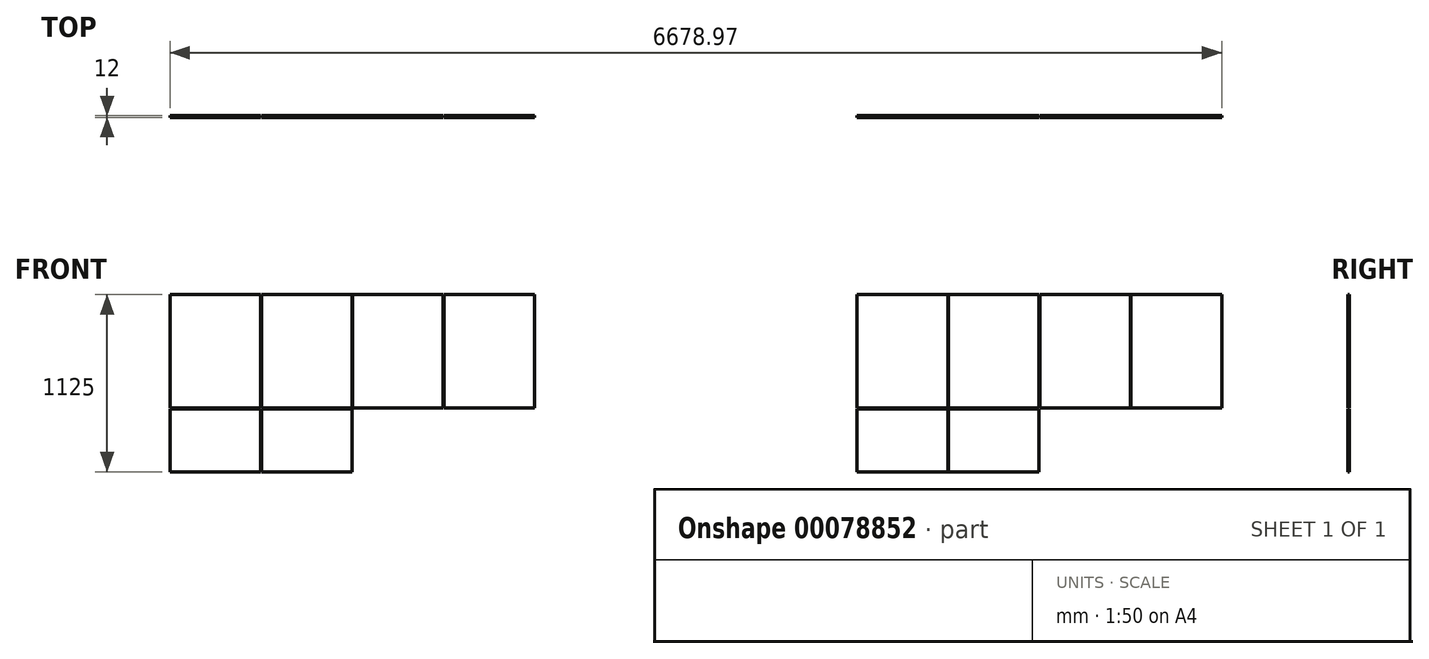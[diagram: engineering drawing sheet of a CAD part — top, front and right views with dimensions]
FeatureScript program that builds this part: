
annotation { "Feature Type Name" : "Feature", "Feature Type Description" : "" }
export const myFeature = defineFeature(function(context is Context, id is Id, definition is map)
    precondition{}
    {
        {
            var Q0;
            Q0=qCreatedBy(makeId("Front.planeOp"),FACE);
            var sketch = newSketch(context, id + "F0", { "sketchPlane" : qUnion([Q0])});
            skLineSegment(sketch, "E0.bottom", {"start": v(0, 0) * mm, "end": v(2400, 0) * mm, "construction": true});
            skLineSegment(sketch, "E0.top", {"start": v(0, 1200) * mm, "end": v(2400, 1200) * mm, "construction": true});
            skLineSegment(sketch, "E0.left", {"start": v(0, 0) * mm, "end": v(0, 1200) * mm, "construction": true});
            skLineSegment(sketch, "E0.right", {"start": v(2400, 0) * mm, "end": v(2400, 1200) * mm, "construction": true});
            skLineSegment(sketch, "E1.bottom", {"start": v(0, 1200) * mm, "end": v(575, 1200) * mm});
            skLineSegment(sketch, "E1.top", {"start": v(0, 480) * mm, "end": v(575, 480) * mm});
            skLineSegment(sketch, "E1.left", {"start": v(0, 1200) * mm, "end": v(0, 480) * mm});
            skLineSegment(sketch, "E1.right", {"start": v(575, 1200) * mm, "end": v(575, 480) * mm});
            skLineSegment(sketch, "E2.1.0.0", {"start": v(580, 480) * mm, "end": v(1155, 480) * mm});
            skLineSegment(sketch, "E2.1.0.1", {"start": v(580, 1200) * mm, "end": v(580, 480) * mm});
            skLineSegment(sketch, "E2.1.0.2", {"start": v(580, 1200) * mm, "end": v(1155, 1200) * mm});
            skLineSegment(sketch, "E2.1.0.3", {"start": v(1155, 1200) * mm, "end": v(1155, 480) * mm});
            skLineSegment(sketch, "E2.2.0.0", {"start": v(1160, 480) * mm, "end": v(1735, 480) * mm});
            skLineSegment(sketch, "E2.2.0.1", {"start": v(1160, 1200) * mm, "end": v(1160, 480) * mm});
            skLineSegment(sketch, "E2.2.0.2", {"start": v(1160, 1200) * mm, "end": v(1735, 1200) * mm});
            skLineSegment(sketch, "E2.2.0.3", {"start": v(1735, 1200) * mm, "end": v(1735, 480) * mm});
            skLineSegment(sketch, "E2.direction1", {"start": v(575, 480) * mm, "end": v(1155, 480) * mm, "construction": true});
            skLineSegment(sketch, "E3.0.3.0", {"start": v(1740, 480) * mm, "end": v(2315, 480) * mm});
            skLineSegment(sketch, "E3.3.3.0", {"start": v(1740, 1200) * mm, "end": v(1740, 480) * mm});
            skLineSegment(sketch, "E3.6.3.0", {"start": v(1740, 1200) * mm, "end": v(2315, 1200) * mm});
            skLineSegment(sketch, "E3.9.3.0", {"start": v(2315, 1200) * mm, "end": v(2315, 480) * mm});
            skLineSegment(sketch, "E4.bottom", {"start": v(0, 475) * mm, "end": v(575, 475) * mm});
            skLineSegment(sketch, "E4.top", {"start": v(0, 75) * mm, "end": v(575, 75) * mm});
            skLineSegment(sketch, "E4.left", {"start": v(0, 475) * mm, "end": v(0, 75) * mm});
            skLineSegment(sketch, "E4.right", {"start": v(575, 475) * mm, "end": v(575, 75) * mm});
            skLineSegment(sketch, "E5.bottom", {"start": v(580, 475) * mm, "end": v(1155, 475) * mm});
            skLineSegment(sketch, "E5.top", {"start": v(580, 75) * mm, "end": v(1155, 75) * mm});
            skLineSegment(sketch, "E5.left", {"start": v(580, 475) * mm, "end": v(580, 75) * mm});
            skLineSegment(sketch, "E5.right", {"start": v(1155, 475) * mm, "end": v(1155, 75) * mm});
            skLineSegment(sketch, "E6", {"start": v(0, 1350) * mm, "end": v(4797.92, 1350) * mm, "construction": true});
            skLineSegment(sketch, "E7.bottom", {"start": v(4363.97, 0) * mm, "end": v(6763.97, 0) * mm, "construction": true});
            skLineSegment(sketch, "E7.top", {"start": v(4363.97, 1200) * mm, "end": v(6763.97, 1200) * mm, "construction": true});
            skLineSegment(sketch, "E7.left", {"start": v(4363.97, 0) * mm, "end": v(4363.97, 1200) * mm, "construction": true});
            skLineSegment(sketch, "E7.right", {"start": v(6763.97, 0) * mm, "end": v(6763.97, 1200) * mm, "construction": true});
            skLineSegment(sketch, "E8.bottom", {"start": v(4363.97, 1200) * mm, "end": v(4938.97, 1200) * mm});
            skLineSegment(sketch, "E8.top", {"start": v(4363.97, 480) * mm, "end": v(4938.97, 480) * mm});
            skLineSegment(sketch, "E8.left", {"start": v(4363.97, 1200) * mm, "end": v(4363.97, 480) * mm});
            skLineSegment(sketch, "E8.right", {"start": v(4938.97, 1200) * mm, "end": v(4938.97, 480) * mm});
            skLineSegment(sketch, "E9.1.0.0", {"start": v(4943.97, 480) * mm, "end": v(5518.97, 480) * mm});
            skLineSegment(sketch, "E9.1.0.1", {"start": v(4943.97, 1200) * mm, "end": v(4943.97, 480) * mm});
            skLineSegment(sketch, "E9.1.0.2", {"start": v(4943.97, 1200) * mm, "end": v(5518.97, 1200) * mm});
            skLineSegment(sketch, "E9.1.0.3", {"start": v(5518.97, 1200) * mm, "end": v(5518.97, 480) * mm});
            skLineSegment(sketch, "E9.2.0.0", {"start": v(5523.97, 480) * mm, "end": v(6098.97, 480) * mm});
            skLineSegment(sketch, "E9.2.0.1", {"start": v(5523.97, 1200) * mm, "end": v(5523.97, 480) * mm});
            skLineSegment(sketch, "E9.2.0.2", {"start": v(5523.97, 1200) * mm, "end": v(6098.97, 1200) * mm});
            skLineSegment(sketch, "E9.2.0.3", {"start": v(6098.97, 1200) * mm, "end": v(6098.97, 480) * mm});
            skLineSegment(sketch, "E9.direction1", {"start": v(4938.97, 480) * mm, "end": v(5518.97, 480) * mm, "construction": true});
            skLineSegment(sketch, "E10.0.3.0", {"start": v(6103.97, 480) * mm, "end": v(6678.97, 480) * mm});
            skLineSegment(sketch, "E10.3.3.0", {"start": v(6103.97, 1200) * mm, "end": v(6103.97, 480) * mm});
            skLineSegment(sketch, "E10.6.3.0", {"start": v(6103.97, 1200) * mm, "end": v(6678.97, 1200) * mm});
            skLineSegment(sketch, "E10.9.3.0", {"start": v(6678.97, 1200) * mm, "end": v(6678.97, 480) * mm});
            skLineSegment(sketch, "E11.bottom", {"start": v(4363.97, 475) * mm, "end": v(4938.97, 475) * mm});
            skLineSegment(sketch, "E11.top", {"start": v(4363.97, 75) * mm, "end": v(4938.97, 75) * mm});
            skLineSegment(sketch, "E11.left", {"start": v(4363.97, 475) * mm, "end": v(4363.97, 75) * mm});
            skLineSegment(sketch, "E11.right", {"start": v(4938.97, 475) * mm, "end": v(4938.97, 75) * mm});
            skLineSegment(sketch, "E12.bottom", {"start": v(4943.97, 475) * mm, "end": v(5518.97, 475) * mm});
            skLineSegment(sketch, "E12.top", {"start": v(4943.97, 75) * mm, "end": v(5518.97, 75) * mm});
            skLineSegment(sketch, "E12.left", {"start": v(4943.97, 475) * mm, "end": v(4943.97, 75) * mm});
            skLineSegment(sketch, "E12.right", {"start": v(5518.97, 475) * mm, "end": v(5518.97, 75) * mm});
            skLineSegment(sketch, "E13", {"start": v(-1376.47, 1350) * mm, "end": v(-533.38, 1350) * mm, "construction": true});
            skSolve(sketch);
        }
        {
            var Q0;
            Q0 = qSketchRegion(id + "F0", true);
            extrude(context, id + "F1", {"entities" : qUnion([Q0]), "depth" : 12 * mm});
        }
    });
